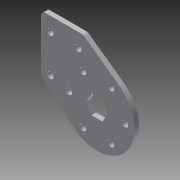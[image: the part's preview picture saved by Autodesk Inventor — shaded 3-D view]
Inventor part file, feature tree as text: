
AUTODESK INVENTOR PART (.ipt)
format: ipt  version: 2014 (Build 180170000, 170)  size: 129,536 bytes
history: native  units: in
note: dims shown in document units (in); Inventor stores cm internally (conversion verified against a paired STEP export)
features: extrude x1, fillet x1
ambient origin geometry x8: Origin, YZ Plane, XZ Plane, XY Plane, X Axis, Y Axis, Z Axis, Center Point
bodies: Solid1 (feature_tree)
feature tree (2):
  extrude  "Extrusion1"  Depth=2.0in
  fillet  "Fillet1"  Radius=0.164in
